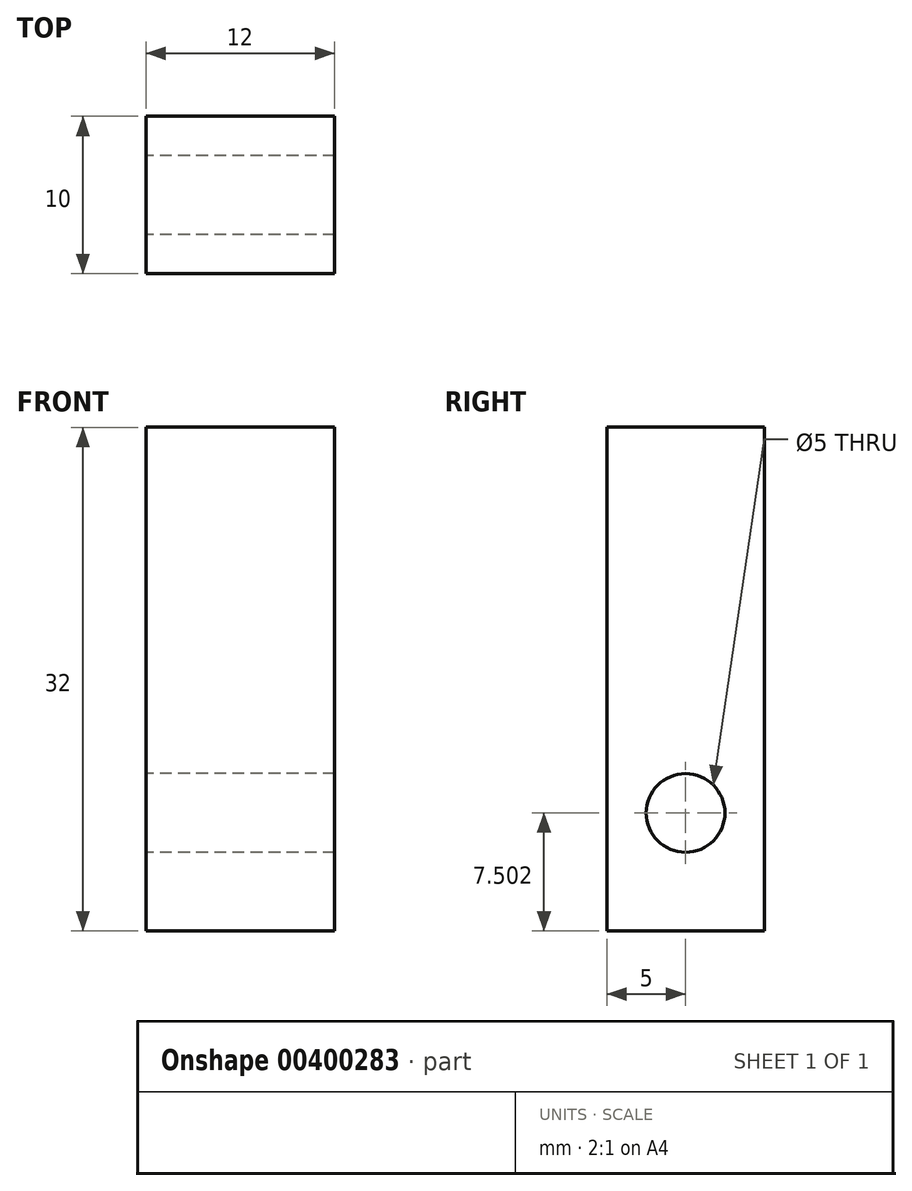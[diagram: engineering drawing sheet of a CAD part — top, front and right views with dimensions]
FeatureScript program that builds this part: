
annotation { "Feature Type Name" : "Feature", "Feature Type Description" : "" }
export const myFeature = defineFeature(function(context is Context, id is Id, definition is map)
    precondition{}
    {
        {
            var Q0;
            Q0=qCreatedBy(makeId("Front.planeOp"),FACE);
            var sketch = newSketch(context, id + "F0", { "sketchPlane" : qUnion([Q0])});
            skLineSegment(sketch, "E0.bottom", {"start": v(-12.89, 17.77) * mm, "end": v(-0.89, 17.77) * mm});
            skLineSegment(sketch, "E0.top", {"start": v(-12.89, -14.23) * mm, "end": v(-0.89, -14.23) * mm});
            skLineSegment(sketch, "E0.left", {"start": v(-12.89, 17.77) * mm, "end": v(-12.89, -14.23) * mm});
            skLineSegment(sketch, "E0.right", {"start": v(-0.89, 17.77) * mm, "end": v(-0.89, -14.23) * mm});
            skSolve(sketch);
        }
        {
            var Q0;
            Q0=makeQuery(id+"F0.imprint","IMPRINT",FACE,{"disambiguationData":[TD([[makeQuery(id+"F0.imprint","IMPRINT",EDGE,{"derivedFrom":sQuery(id+"F0.wireOp",EDGE,"E0.bottom")}),-1.0]])]});
            extrude(context, id + "F1", {"entities" : qUnion([Q0]), "depth" : 10 * mm});
        }
        {
            var Q0;
            Q0=makeQuery(id+"F1.opExtrude","SWEPT_FACE",FACE,{"disambiguationData":[OSD([sQuery(id+"F0.wireOp",EDGE,"E0.left")])]});
            var sketch = newSketch(context, id + "F2", { "sketchPlane" : qUnion([Q0])});
            skCircle(sketch, "E1", {"center": v(5, -6.73) * mm, "radius": 2.5 * mm});
            skSolve(sketch);
        }
        {
            var Q0;
            Q0=makeQuery(id+"F2.imprint","IMPRINT",FACE,{"disambiguationData":[TD([[makeQuery(id+"F2.imprint","IMPRINT",EDGE,{"derivedFrom":sQuery(id+"F2.wireOp",EDGE,"E1")}),1.0]])]});
            extrude(context, id + "F3", {"entities" : qUnion([Q0]), "operationType" : NewBodyOperationType.REMOVE, "oppositeDirection" : true, "depth" : 25 * mm});
        }
    });
